# Revit family: zzzFaucet_Kitchen-Single_Handle-Grohe-Zedra-32283_Series
name_source: partatom
category: Plumbing Fixtures
units: mm (PartAtom-declared; Revit-internal decimal feet)

## family parameters
Always vertical = No
Cut with Voids When Loaded = No
OmniClass Number = 23.45.55.14
OmniClass Title = Single Faucets
Part Type = Normal
Room Calculation Point = No
Round Connector Dimension = Use Diameter
Shared = Yes
Work Plane-Based = Yes

## types (2) — shared parameters
ADA Compliant = Yes
ASME A112.18.1/CSA B125.1 = Yes
Assembly Code = D2020300
CEC Compliant = Yes
CW Connection = No
CWFU = 1.5
CalGreen Compliant = Yes
Compliance Certifications = Low Lead Certified, Massachusetts Plumbing Board Approved, NSF 61, CSA B125.1 & Complies with lead plumbing laws
Default Elevation = 0"
Description = Single-Handle Pull Down Dual Spray Prep Faucet 6.6/min (1.75 gpm)
Energy Policy Act of 1992 = Yes
Flow Rate = 1.75 gpm (6.6 L/min)
HW Connection = No
HWFU = 1.5
Height = 15 7/16"
Height- Spout = 9"
Installation Instruction Link = https://americanstandard.box.com
Installation Type = Deck-Mounted
Laminar (LAM) = Yes
Length = 6 9/16"
Manufacturer = Grohe
Price = Prices may vary. Please consult Manufacturer Representative for most up-to-date price list.
Product Documentation Link = https://americanstandard.box.com
Product Page URL = https://www.grohe.us
Revised Date = 03/01/2022
Tempered Water Connection = Yes
Tempered Water Connection Diameter = 3/8"
URL = https://www.grohe.us
Vent Connection = No
WFU = 2
Warranty Information = Lifetime Limited Warranty

## per-type parameters (varying)
| type | Finish | Material | Waste Connection | Width |
| 32283003 | Zinc-Grohe-003-StarLight Chrome | Zinc-Grohe-003-StarLight Chrome | No | 5 1/2" |
| 32283DC3 | Zinc-Grohe-DC3-SuperSteel Infinity Finish | Zinc-Grohe-DC3-SuperSteel Infinity Finish | Yes | 2 3/8" |

note: column(s) folded — value = type name in every type: Model

## geometry (parser evidence)
native form markers: Sweep x2
no freeform markers — native parametric forms only
